# Revit family: 13506e
name_source: partatom
category: Systemy meblowe
units: mm (PartAtom-declared; Revit-internal decimal feet)

## family parameters
Oparty na płaszczyźnie roboczej = Nie
Punkt obliczania pomieszczeń = Nie
Tnij formami wycięć po wczytaniu = Nie
Typ części = Normalny
Współdzielony = Nie
Wymiar okrągłego złącza = Użyj średnicy
Włącz cięcie w widokach = Nie
Zawsze pionowo = Tak

## types (1)
- 13506e
    Critical falling height = 205 cm
    Domyślna rzędna = 0 cm
    Height = 210 cm
    Hosted on larslaj.com = https://larslaj.com
    LARSLAJ_materials = larslaj.com/bim
    Lenght = 155 cm
    Maintenance = We recommend to examine and tighten all screws and bolt clamps after a few weeks’ use. In order to prevent cracks and to extend the life of the wood, it is recommended that the wood details should be oiled every 3-5 years.
    Material = Larch, stainless steel, powder coated steel
    Model = 13506e
    Producent = Lars Laj
    Product Groups = Ural Eco
    Product line = Nature Nordic Swan Ecolabel
    Steel = <Wg kategorii>
    URL = https://www.larslaj.com
    Width = 672 cm
    Wood = <Wg kategorii>
